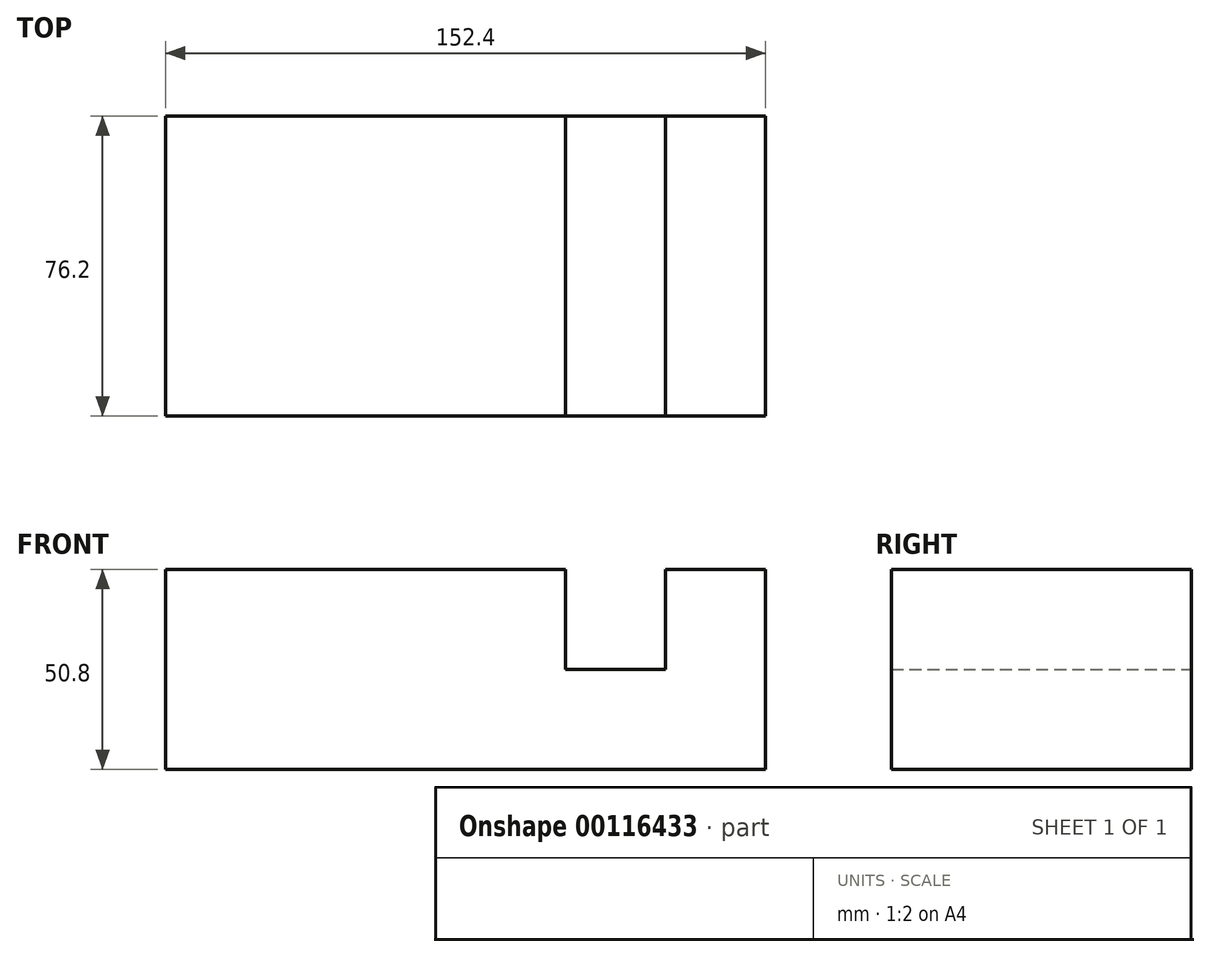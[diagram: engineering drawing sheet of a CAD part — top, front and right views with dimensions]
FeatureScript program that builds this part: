
annotation { "Feature Type Name" : "Feature", "Feature Type Description" : "" }
export const myFeature = defineFeature(function(context is Context, id is Id, definition is map)
    precondition{}
    {
        {
            var Q0;
            Q0=qCreatedBy(makeId("Front.planeOp"),FACE);
            var sketch = newSketch(context, id + "F0", { "sketchPlane" : qUnion([Q0])});
            skLineSegment(sketch, "E0", {"start": v(0, 0) * mm, "end": v(152.4, 0) * mm});
            skLineSegment(sketch, "E1", {"start": v(152.4, 0) * mm, "end": v(152.4, 50.8) * mm});
            skLineSegment(sketch, "E2", {"start": v(152.4, 50.8) * mm, "end": v(127, 50.8) * mm});
            skLineSegment(sketch, "E3", {"start": v(127, 50.8) * mm, "end": v(127, 25.4) * mm});
            skLineSegment(sketch, "E4", {"start": v(127, 25.4) * mm, "end": v(101.6, 25.4) * mm});
            skLineSegment(sketch, "E5", {"start": v(101.6, 25.4) * mm, "end": v(101.6, 50.8) * mm});
            skLineSegment(sketch, "E6", {"start": v(101.6, 50.8) * mm, "end": v(0, 50.8) * mm});
            skLineSegment(sketch, "E7", {"start": v(0, 50.8) * mm, "end": v(0, 0) * mm});
            skSolve(sketch);
        }
        {
            var Q0;
            Q0=makeQuery(id+"F0.imprint","IMPRINT",FACE,{"disambiguationData":[TD([[makeQuery(id+"F0.imprint","IMPRINT",EDGE,{"derivedFrom":sQuery(id+"F0.wireOp",EDGE,"E0")}),1.0]])]});
            extrude(context, id + "F1", {"entities" : qUnion([Q0]), "depth" : 76.2 * mm});
        }
    });
